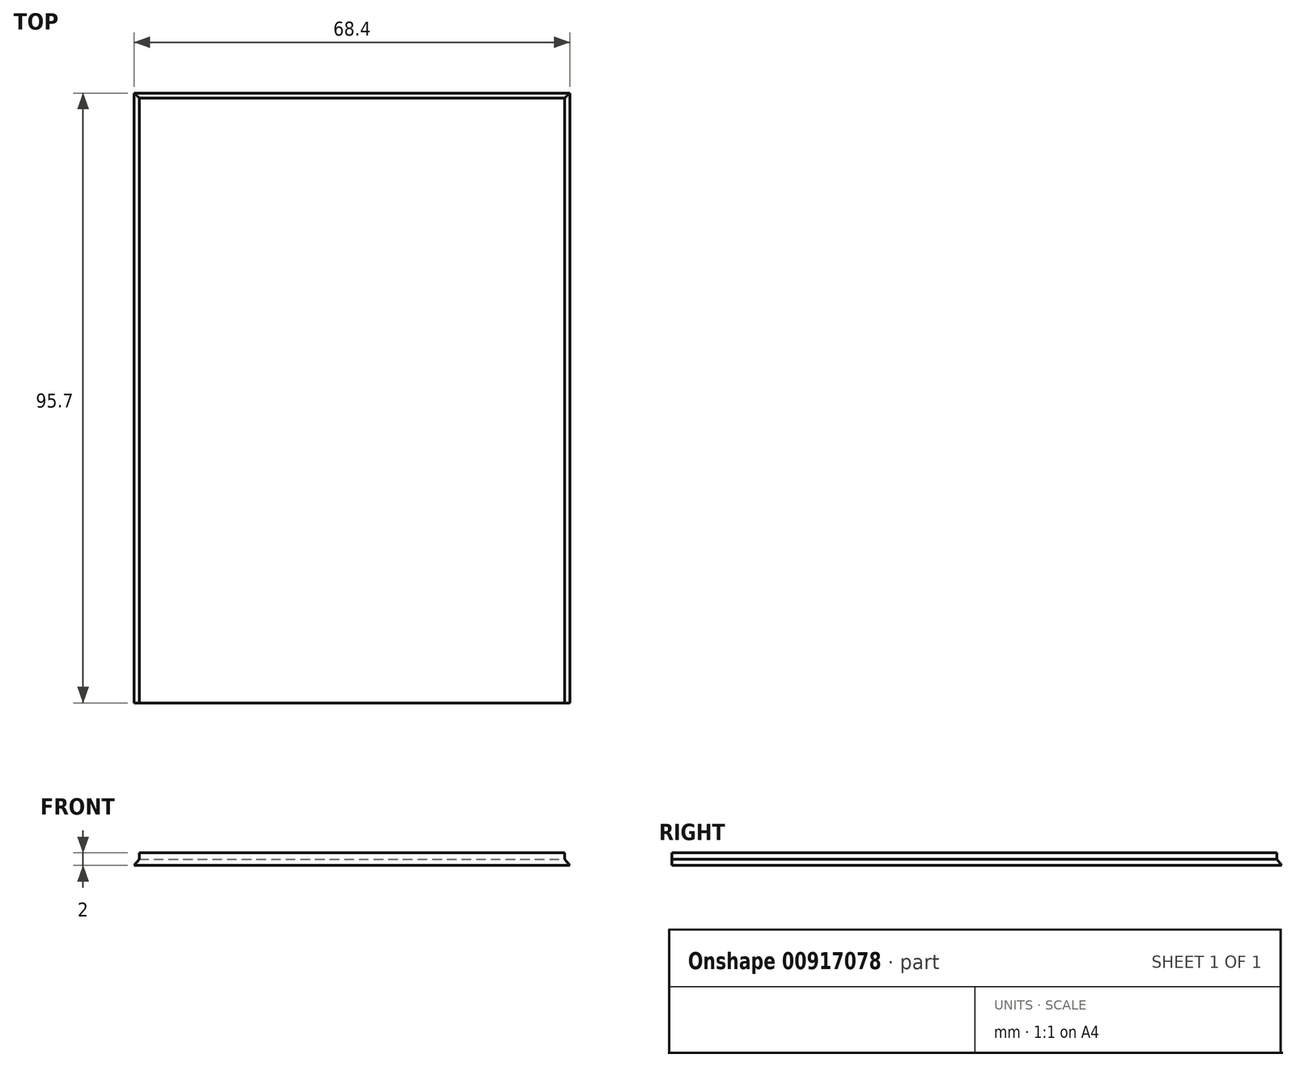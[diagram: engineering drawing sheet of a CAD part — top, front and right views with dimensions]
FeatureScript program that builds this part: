
annotation { "Feature Type Name" : "Feature", "Feature Type Description" : "" }
export const myFeature = defineFeature(function(context is Context, id is Id, definition is map)
    precondition{}
    {
        {
            var Q0;
            Q0=qCreatedBy(makeId("Front.planeOp"),FACE);
            var sketch = newSketch(context, id + "F0", { "sketchPlane" : qUnion([Q0])});
            skLineSegment(sketch, "E0", {"start": v(0.8, 1) * mm, "end": v(0.8, 2) * mm});
            skLineSegment(sketch, "E1", {"start": v(0.8, 2) * mm, "end": v(67.6, 2) * mm});
            skLineSegment(sketch, "E2", {"start": v(67.6, 2) * mm, "end": v(67.6, 1) * mm});
            skLineSegment(sketch, "E3", {"start": v(68.4, 0) * mm, "end": v(0, 0) * mm});
            skLineSegment(sketch, "E4", {"start": v(0, 0) * mm, "end": v(0.8, 1) * mm});
            skLineSegment(sketch, "E5", {"start": v(67.6, 1) * mm, "end": v(68.4, 0) * mm});
            skSolve(sketch);
        }
        {
            var Q0;
            Q0=qSketchRegion(id+"F0",true);
            extrude(context, id + "F1", {"entities" : qUnion([Q0]), "oppositeDirection" : true, "depth" : 96.9 * mm, "offsetDistance" : 25 * mm});
        }
        {
            var Q0;
            Q0=makeQuery(id+"F1.opExtrude","SWEPT_FACE",FACE,{"disambiguationData":[OSD([sQuery(id+"F0.wireOp",EDGE,"E2")])]});
            var sketch = newSketch(context, id + "F2", { "sketchPlane" : qUnion([Q0])});
            skLineSegment(sketch, "E6", {"start": v(96.9, 2) * mm, "end": v(94.9, 2) * mm});
            skLineSegment(sketch, "E7", {"start": v(94.9, 2) * mm, "end": v(94.9, 1) * mm});
            skLineSegment(sketch, "E8", {"start": v(94.9, 1) * mm, "end": v(95.7, 0) * mm});
            skLineSegment(sketch, "E9", {"start": v(95.7, 0) * mm, "end": v(96.9, 0) * mm});
            skLineSegment(sketch, "E10", {"start": v(96.9, 0) * mm, "end": v(96.9, 2) * mm});
            skSolve(sketch);
        }
        {
            var Q0;
            Q0 = qSketchRegion(id + "F2", true);
            extrude(context, id + "F3", {"entities" : qUnion([Q0]), "operationType" : NewBodyOperationType.REMOVE, "endBound" : BoundingType.SYMMETRIC, "oppositeDirection" : true, "depth" : 148.4 * mm, "offsetDistance" : 25 * mm});
        }
    });
